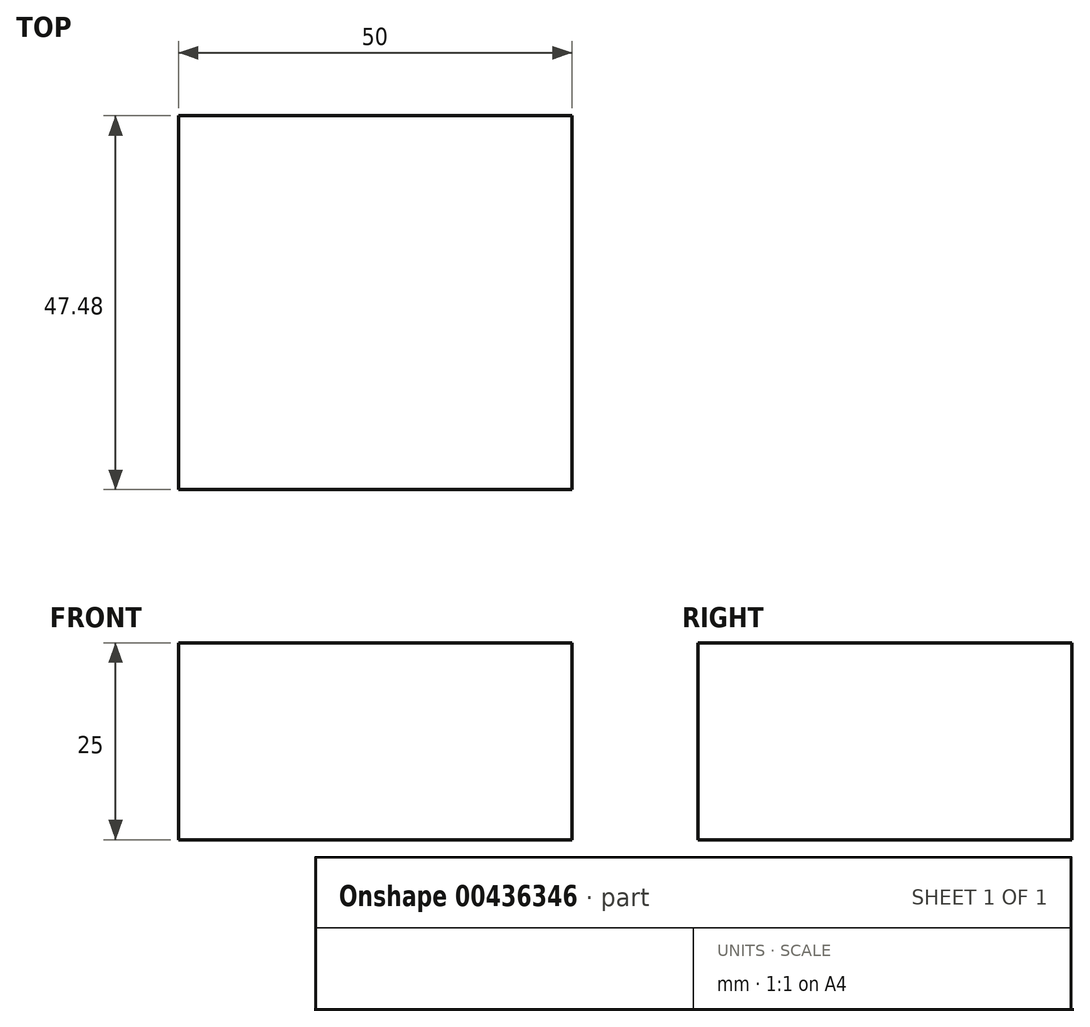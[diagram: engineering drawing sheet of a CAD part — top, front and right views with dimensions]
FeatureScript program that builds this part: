
annotation { "Feature Type Name" : "Feature", "Feature Type Description" : "" }
export const myFeature = defineFeature(function(context is Context, id is Id, definition is map)
    precondition{}
    {
        {
            var Q0;
            Q0=qCreatedBy(makeId("Top.planeOp"),FACE);
            var sketch = newSketch(context, id + "F0", { "sketchPlane" : qUnion([Q0])});
            skLineSegment(sketch, "E0.bottom", {"start": v(25.94, 42.76) * mm, "end": v(75.94, 42.76) * mm});
            skLineSegment(sketch, "E0.top", {"start": v(25.94, 90.24) * mm, "end": v(75.94, 90.24) * mm});
            skLineSegment(sketch, "E0.left", {"start": v(25.94, 42.76) * mm, "end": v(25.94, 90.24) * mm});
            skLineSegment(sketch, "E0.right", {"start": v(75.94, 42.76) * mm, "end": v(75.94, 90.24) * mm});
            skSolve(sketch);
        }
        {
            var Q0;
            Q0=makeQuery(id+"F0.imprint","IMPRINT",FACE,{"disambiguationData":[TD([[makeQuery(id+"F0.imprint","IMPRINT",EDGE,{"derivedFrom":sQuery(id+"F0.wireOp",EDGE,"E0.bottom")}),1.0]])]});
            extrude(context, id + "F1", {"entities" : qUnion([Q0]), "depth" : 25 * mm});
        }
    });
